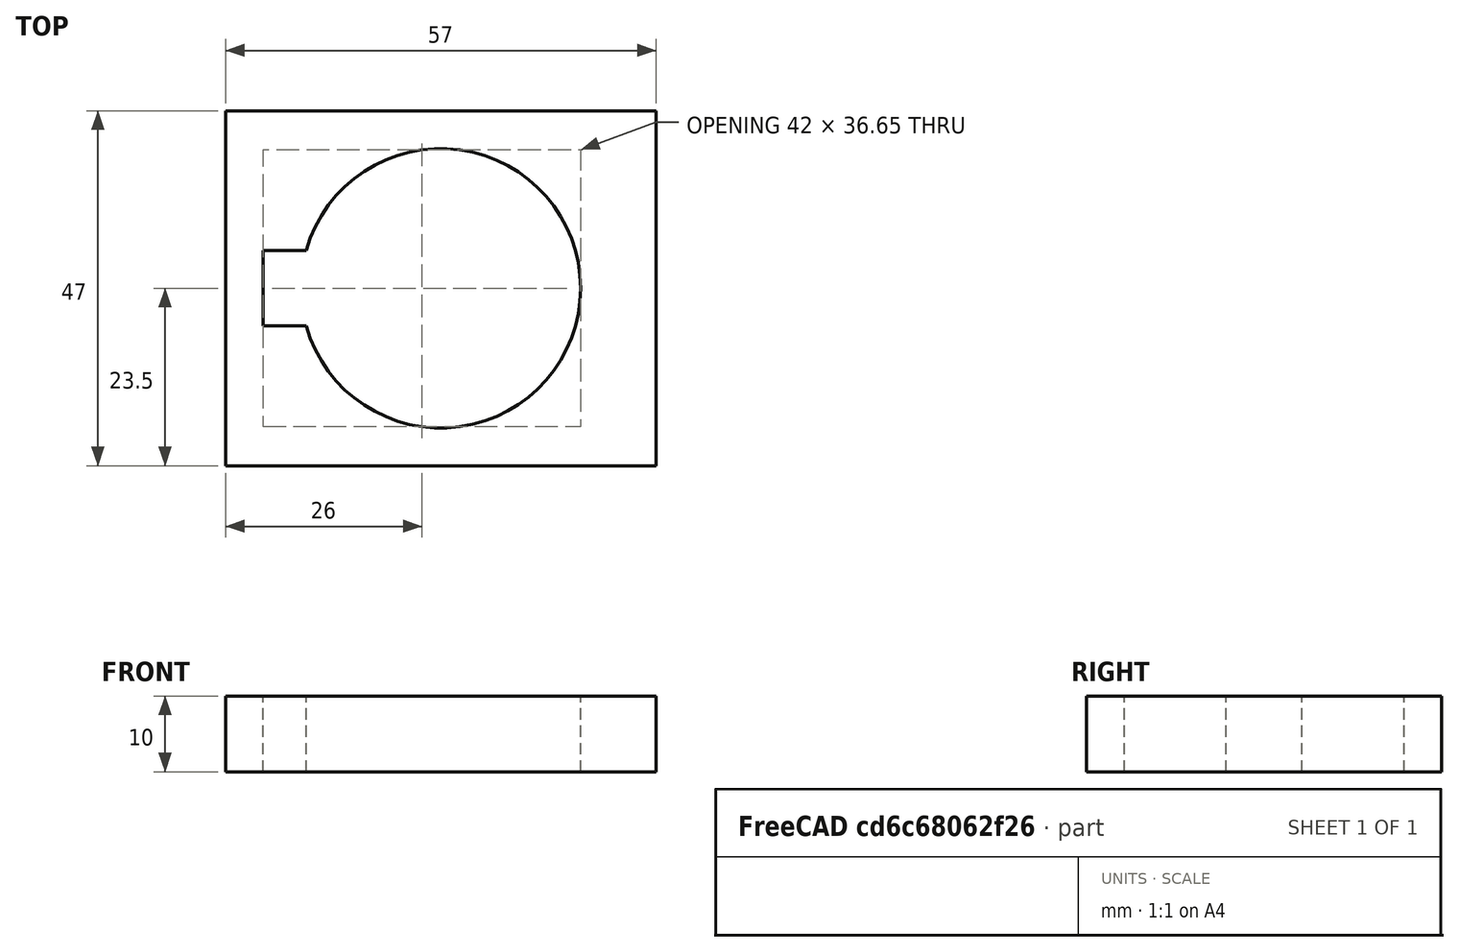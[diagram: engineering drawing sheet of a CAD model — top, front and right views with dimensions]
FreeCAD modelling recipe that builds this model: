
FCSTD DOCUMENT  (FreeCAD 0.17R13522 (Git))
Label: fastener-join-37mm
License: All rights reserved
LicenseURL: http://en.wikipedia.org/wiki/All_rights_reserved
objects: Part::Box×2, Part::Cylinder×1, Part::MultiFuse×1, Part::Cut×1
note: 5 computed .brp shape members not serialized (recipe doc carries the construction recipe); baked Part::Feature solids carry a one-line shape summary decoded from their .brp

FEATURE [Part::Box] Box  label="Cube"
  AttacherType = Attacher::AttachEngine3D
  Height = 10
  Length = 57
  Placement = pos=(-10,-23.5,-5) rot=(0,0,1;0rad)
  Width = 47
FEATURE [Part::Cylinder] Cylinder
  Angle = 360
  AttacherType = Attacher::AttachEngine3D
  Height = 10
  Placement = pos=(18.5,0,-5) rot=(0,0,1;0rad)
  Radius = 18.5
FEATURE [Part::Box] Box001  label="Cube001"
  AttacherType = Attacher::AttachEngine3D
  Height = 10
  Length = 10
  Placement = pos=(-5,-5,-5) rot=(0,0,1;0rad)
  Width = 10
FEATURE [Part::MultiFuse] Fusion
  Shapes = -> [Box001,Cylinder]
FEATURE [Part::Cut] Cut
  Base = -> Box
  Tool = -> Fusion
